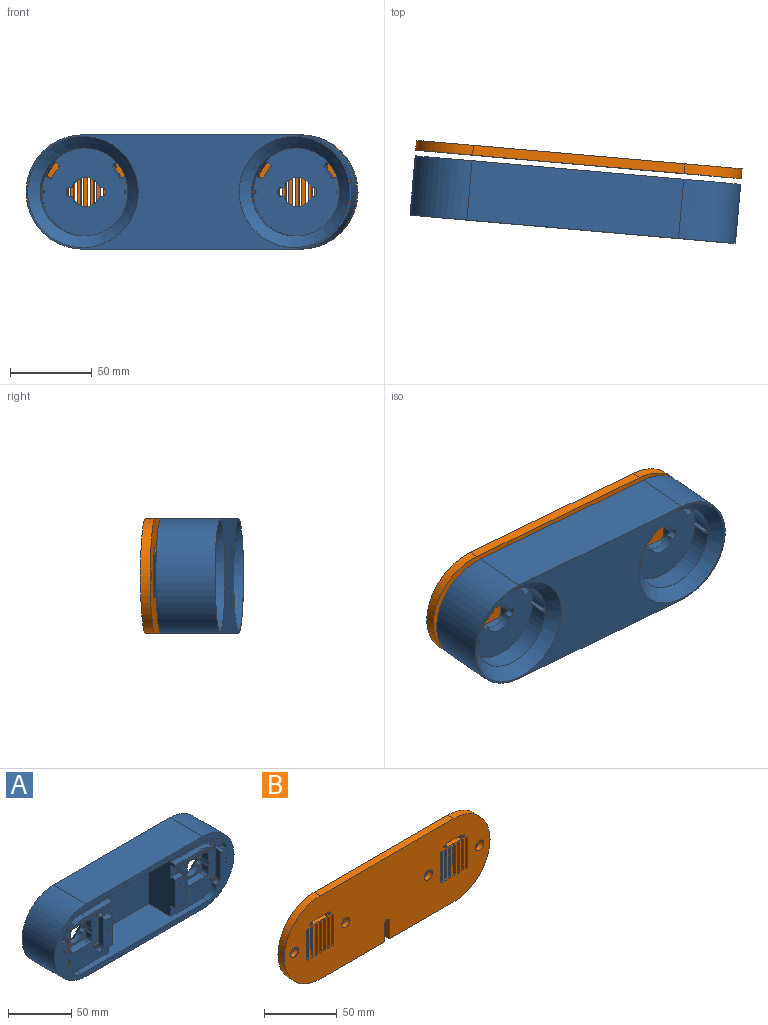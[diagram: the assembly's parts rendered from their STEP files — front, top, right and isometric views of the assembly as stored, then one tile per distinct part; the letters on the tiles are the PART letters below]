
ASSEMBLY  parts=2 mates=1
PART A: 163 faces, bbox 200x36.4x70 mm
  f0: plane 12.01x2.86mm, normal (0.7,0,-0.71), area 45.9mm2, adj f10,f16,f24,f27,f94,f131,f132,f159
  f1: plane 12.01x2.86mm, normal (-0.7,0,-0.71), area 45.9mm2, adj f11,f17,f24,f27,f93,f133,f134,f154
  f2: plane 12.01x2.86mm, normal (0.7,0,-0.71), area 45.9mm2, adj f13,f18,f21,f26,f108,f119,f120,f150
  f3: plane 12.01x2.86mm, normal (-0.7,0,-0.71), area 45.9mm2, adj f15,f19,f21,f26,f105,f123,f124,f145
  f4: plane 41.23x3mm, normal (0,-1,0), area 112.8mm2, adj f8,f78,f147,f148
  f5: plane 30.73x14.5mm, normal (0,-1,0), area 285.2mm2, adj f9,f17,f83,f84,f85,f138,f153
  f6: plane 30.73x14.5mm, normal (0,-1,0), area 285.2mm2, adj f8,f18,f79,f80,f81,f140,f151
  f7: plane 200x70mm, normal (0,-1,0), area 2873.6mm2, adj f16,f19,f37,f38,f39,f40,f70,f71
  f8: plane 60x30.4mm, normal (1,0,0), area 1662.8mm2, adj f4,f6,f26,f73,f78,f81,f82,f90
  f9: plane 60x30.4mm, normal (-1,0,0), area 1662.8mm2, adj f5,f27,f28,f73,f82,f83,f86,f90
  f10: cylinder r=26.5mm len=11.9mm, axis (0,1,0), area 131.3mm2, adj f0,f24,f88,f162
  f11: cylinder r=26.5mm len=11.9mm, axis (0,1,0), area 131.3mm2, adj f1,f12,f24,f155
  f12: plane 11.9x3.74mm, normal (0.36,0,0.93), area 47.6mm2, adj f11,f17,f24,f155
  f13: cylinder r=26.5mm len=11.9mm, axis (0,1,0), area 131.3mm2, adj f2,f14,f21,f152
  f14: plane 11.9x3.74mm, normal (-0.36,0,0.93), area 47.6mm2, adj f13,f18,f21,f152
  f15: cylinder r=26.5mm len=11.9mm, axis (0,1,0), area 131.3mm2, adj f3,f21,f89,f149
  f16: cylinder r=22.5mm len=17.4mm, axis (0,1,0), area 128mm2, adj f0,f7,f24,f27,f87,f88,f94,f131
  f17: cylinder r=22.5mm len=17.4mm, axis (0,1,0), area 128mm2, adj f1,f5,f12,f24,f27,f85,f93,f133
  f18: cylinder r=22.5mm len=17.4mm, axis (0,1,0), area 128mm2, adj f2,f6,f14,f21,f26,f79,f108,f119
  f19: cylinder r=22.5mm len=17.4mm, axis (0,1,0), area 128mm2, adj f3,f7,f21,f26,f77,f89,f105,f123
  f20: cylinder r=27mm len=53.98mm, axis (0,1,0), area 999.9mm2, adj f21,f42,f115,f117
  f21: plane 54x54mm, normal (0,1,0), area 1917.8mm2, adj f2,f3,f13,f14,f15,f18,f19,f20
  f22: cylinder r=27mm len=53.98mm, axis (0,1,0), area 999.9mm2, adj f21,f42,f115,f117
  f23: cylinder r=27mm len=53.98mm, axis (0,1,0), area 999.9mm2, adj f24,f43,f111,f113
  f24: plane 54x54mm, normal (0,1,0), area 1917.8mm2, adj f0,f1,f10,f11,f12,f16,f17,f23
  f25: cylinder r=27mm len=53.98mm, axis (0,1,0), area 999.9mm2, adj f24,f43,f111,f113
  f26: plane 49.5x49.5mm, normal (0,-1,0), area 1345mm2, adj f2,f3,f8,f18,f19,f44,f45,f46
  f27: plane 49.5x49.5mm, normal (0,-1,0), area 1345mm2, adj f0,f1,f9,f16,f17,f58,f59,f60
  f28: plane 41.23x3mm, normal (0,-1,0), area 112.8mm2, adj f9,f86,f156,f157
  f29: cylinder r=3mm len=6mm, axis (0,-1,0), area 52.9mm2, adj f24,f30,f32,f57
  f30: cylinder r=9mm len=17.01mm, axis (0,-1,0), area 111.4mm2, adj f24,f29,f31,f57
  f31: cylinder r=3mm len=6mm, axis (0,-1,0), area 52.9mm2, adj f24,f30,f32,f57
  f32: cylinder r=9mm len=17.01mm, axis (0,-1,0), area 111.4mm2, adj f24,f29,f31,f57
  f33: cylinder r=3mm len=6mm, axis (0,-1,0), area 52.9mm2, adj f21,f34,f36,f56
  f34: cylinder r=9mm len=17.01mm, axis (0,-1,0), area 111.4mm2, adj f21,f33,f35,f56
  f35: cylinder r=3mm len=6mm, axis (0,-1,0), area 52.9mm2, adj f21,f34,f36,f56
  f36: cylinder r=9mm len=17.01mm, axis (0,-1,0), area 111.4mm2, adj f21,f33,f35,f56
  f37: cylinder r=35mm len=70mm, axis (0,-1,0), area 4002.4mm2, adj f7,f38,f40,f41
  f38: plane 130x36.4mm, normal (0,0,-1), area 4732mm2, adj f7,f37,f39,f41
  f39: cylinder r=35mm len=70mm, axis (0,-1,0), area 4002.4mm2, adj f7,f38,f40,f41
  f40: plane 130x36.4mm, normal (0,0,1), area 4732mm2, adj f7,f37,f39,f41
  f41: plane 200x70mm, normal (0,1,0), area 5685.1mm2, adj f37,f38,f39,f40,f42,f43
  f42: cone r=27mm half-angle=45deg, axis (0,1,0), area 1897.1mm2, adj f20,f22,f41,f116,f118
  f43: cone r=27mm half-angle=45deg, axis (0,1,0), area 1897.1mm2, adj f23,f25,f41,f112,f114
  f44: cylinder r=2.7mm len=7mm, axis (0,-1,0), area 29.7mm2, adj f26,f45,f55,f56
  f45: plane 7.5x7mm, normal (1,0,0), area 52.5mm2, adj f26,f44,f46,f56
  f46: cylinder r=3.62mm len=7mm, axis (0,-1,0), area 38.6mm2, adj f26,f45,f47,f56
  f47: plane 7x5.5mm, normal (1,0,0), area 38.5mm2, adj f26,f46,f48,f56
  f48: cylinder r=2.7mm len=7mm, axis (0,-1,0), area 29.7mm2, adj f26,f47,f49,f56
  f49: plane 18x7mm, normal (0,0,1), area 126mm2, adj f26,f48,f50,f56
  f50: cylinder r=2.7mm len=7mm, axis (0,-1,0), area 29.7mm2, adj f26,f49,f51,f56
  f51: plane 7x5.5mm, normal (-1,0,0), area 38.5mm2, adj f26,f50,f52,f56
  f52: cylinder r=3.62mm len=7mm, axis (0,-1,0), area 38.6mm2, adj f26,f51,f53,f56
  f53: plane 7.5x7mm, normal (-1,0,0), area 52.5mm2, adj f26,f52,f54,f56
  f54: cylinder r=2.7mm len=7mm, axis (0,-1,0), area 29.7mm2, adj f26,f53,f55,f56
  f55: plane 18x7mm, normal (0,0,-1), area 126mm2, adj f26,f44,f54,f56
  f56: plane 25.4x23.4mm, normal (0,-1,0), area 262.5mm2, adj f33,f34,f35,f36,f44,f45,f46,f47
  f57: plane 25.4x23.4mm, normal (0,-1,0), area 262.5mm2, adj f29,f30,f31,f32,f58,f59,f60,f61
  f58: cylinder r=2.7mm len=7mm, axis (0,-1,0), area 29.7mm2, adj f27,f57,f59,f69
  f59: plane 18x7mm, normal (0,0,1), area 126mm2, adj f27,f57,f58,f60
  f60: cylinder r=2.7mm len=7mm, axis (0,-1,0), area 29.7mm2, adj f27,f57,f59,f61
  f61: plane 7x5.5mm, normal (-1,0,0), area 38.5mm2, adj f27,f57,f60,f62
  f62: cylinder r=3.62mm len=7mm, axis (0,-1,0), area 38.6mm2, adj f27,f57,f61,f63
  f63: plane 7.5x7mm, normal (-1,0,0), area 52.5mm2, adj f27,f57,f62,f64
  f64: cylinder r=2.7mm len=7mm, axis (0,-1,0), area 29.7mm2, adj f27,f57,f63,f65
  f65: plane 18x7mm, normal (0,0,-1), area 126mm2, adj f27,f57,f64,f66
  f66: cylinder r=2.7mm len=7mm, axis (0,-1,0), area 29.7mm2, adj f27,f57,f65,f67
  f67: plane 7.5x7mm, normal (1,0,0), area 52.5mm2, adj f27,f57,f66,f68
  f68: cylinder r=3.62mm len=7mm, axis (0,-1,0), area 38.6mm2, adj f27,f57,f67,f69
  f69: plane 7x5.5mm, normal (1,0,0), area 38.5mm2, adj f27,f57,f58,f68
  f70: cylinder r=4mm len=5.4mm, axis (0,1,0), area 33.9mm2, adj f7,f27,f71,f87
  f71: plane 5.4x0.5mm, normal (-1,0,0), area 2.7mm2, adj f7,f27,f70,f72
  f72: cylinder r=10mm len=10mm, axis (0,1,0), area 84.8mm2, adj f7,f27,f71,f73
  f73: plane 141x30.4mm, normal (0,0,1), area 2511.4mm2, adj f7,f8,f9,f26,f27,f72,f74,f90
  f74: cylinder r=10mm len=10mm, axis (0,1,0), area 84.8mm2, adj f7,f26,f73,f75
  f75: plane 5.4x0.5mm, normal (1,0,0), area 2.7mm2, adj f7,f26,f74,f76
  f76: cylinder r=4mm len=5.4mm, axis (0,1,0), area 33.9mm2, adj f7,f26,f75,f77
  f77: plane 26.73x5.4mm, normal (1,0,0), area 144.3mm2, adj f7,f19,f26,f76
  f78: plane 41.23x5.5mm, normal (0,0,-1), area 224.1mm2, adj f4,f8,f26,f147,f150,f152
  f79: plane 26.73x5.4mm, normal (-1,0,0), area 144.3mm2, adj f6,f18,f26,f80
  f80: cylinder r=4mm len=5.4mm, axis (0,1,0), area 33.9mm2, adj f6,f26,f79,f81
  f81: plane 14.5x5.4mm, normal (0,0,-1), area 78.3mm2, adj f6,f8,f26,f80
  f82: plane 130x30.4mm, normal (0,0,-1), area 2458mm2, adj f7,f8,f9,f90,f143,f149,f161,f162
  f83: plane 14.5x5.4mm, normal (0,0,-1), area 78.3mm2, adj f5,f9,f27,f84
  f84: cylinder r=4mm len=5.4mm, axis (0,1,0), area 33.9mm2, adj f5,f27,f83,f85
  f85: plane 26.73x5.4mm, normal (1,0,0), area 144.3mm2, adj f5,f17,f27,f84
  f86: plane 41.23x5.5mm, normal (0,0,-1), area 224.1mm2, adj f9,f27,f28,f154,f155,f157
  f87: plane 26.73x5.4mm, normal (-1,0,0), area 144.3mm2, adj f7,f16,f27,f70
  f88: plane 17.4x3.74mm, normal (-0.36,0,0.93), area 69.6mm2, adj f7,f10,f16,f24,f160
  f89: plane 17.4x3.74mm, normal (0.36,0,0.93), area 69.6mm2, adj f7,f15,f19,f21,f144
  f90: plane 70x60mm, normal (0,-1,0), area 4200mm2, adj f8,f9,f73,f82
  f91: cylinder r=2mm len=4mm, axis (0,1,0), area 25.1mm2, adj f27,f92,f93
  f92: plane 4x4mm, normal (0,-1,0), area 9.9mm2, adj f91,f134
  f93: plane 2.33x1.26mm, normal (0,1,0), area 1.7mm2, adj f1,f17,f91,f134
  f94: plane 2.33x1.26mm, normal (0,1,0), area 1.7mm2, adj f0,f16,f95,f132
  f95: cylinder r=2mm len=4mm, axis (0,1,0), area 25.1mm2, adj f27,f94,f96
  f96: plane 4x4mm, normal (0,-1,0), area 9.9mm2, adj f95,f132
  f97: cylinder r=2mm len=4mm, axis (0,1,0), area 25.1mm2, adj f27,f98
  f98: plane 4x4mm, normal (0,-1,0), area 9.9mm2, adj f97,f130
  f99: cylinder r=2mm len=4mm, axis (0,1,0), area 25.1mm2, adj f27,f100
  f100: plane 4x4mm, normal (0,-1,0), area 9.9mm2, adj f99,f128
  f101: cylinder r=2mm len=4mm, axis (0,1,0), area 25.1mm2, adj f26,f102
  f102: plane 4x4mm, normal (0,-1,0), area 9.9mm2, adj f101,f126
  f103: cylinder r=2mm len=4mm, axis (0,1,0), area 25.1mm2, adj f26,f104,f105
  f104: plane 4x4mm, normal (0,-1,0), area 9.9mm2, adj f103,f124
  f105: plane 2.33x1.26mm, normal (0,1,0), area 1.7mm2, adj f3,f19,f103,f124
  f106: cylinder r=2mm len=4mm, axis (0,1,0), area 25.1mm2, adj f26,f107
  f107: plane 4x4mm, normal (0,-1,0), area 9.9mm2, adj f106,f122
  f108: plane 2.33x1.26mm, normal (0,1,0), area 1.7mm2, adj f2,f18,f109,f120
  f109: cylinder r=2mm len=4mm, axis (0,1,0), area 25.1mm2, adj f26,f108,f110
  f110: plane 4x4mm, normal (0,-1,0), area 9.9mm2, adj f109,f120
  f111: extruded ~12x1.99mm, area 57.1mm2, adj f23,f24,f25,f112
  f112: plane 2x1.5mm, normal (0,1,0), area 2.6mm2, adj f43,f111
  f113: extruded ~12x1.99mm, area 57.1mm2, adj f23,f24,f25,f114
  f114: plane 2x1.5mm, normal (0,1,0), area 2.6mm2, adj f43,f113
  f115: extruded ~12x1.99mm, area 57.1mm2, adj f20,f21,f22,f116
  f116: plane 2x1.5mm, normal (0,1,0), area 2.6mm2, adj f42,f115
  f117: extruded ~12x1.99mm, area 57.1mm2, adj f20,f21,f22,f118
  f118: plane 2x1.5mm, normal (0,1,0), area 2.6mm2, adj f42,f117
  f119: cone r=0mm half-angle=59deg, axis (0,-1,0), area 3mm2, adj f2,f18,f120
  f120: cylinder r=0.93mm len=8mm, axis (0,-1,0), area 42.2mm2, adj f2,f18,f108,f110,f119
  f121: cone r=0mm half-angle=59deg, axis (0,-1,0), area 3.1mm2, adj f122
  f122: cylinder r=0.93mm len=8mm, axis (0,-1,0), area 46.5mm2, adj f107,f121
  f123: cone r=0mm half-angle=59deg, axis (0,-1,0), area 3mm2, adj f3,f19,f124
  f124: cylinder r=0.93mm len=8mm, axis (0,-1,0), area 42.2mm2, adj f3,f19,f104,f105,f123
  f125: cone r=0mm half-angle=59deg, axis (0,-1,0), area 3.1mm2, adj f126
  f126: cylinder r=0.93mm len=8mm, axis (0,-1,0), area 46.5mm2, adj f102,f125
  f127: cone r=0mm half-angle=59deg, axis (0,-1,0), area 3.1mm2, adj f128
  f128: cylinder r=0.93mm len=8mm, axis (0,-1,0), area 46.5mm2, adj f100,f127
  f129: cone r=0mm half-angle=59deg, axis (0,-1,0), area 3.1mm2, adj f130
  f130: cylinder r=0.93mm len=8mm, axis (0,-1,0), area 46.5mm2, adj f98,f129
  f131: cone r=0mm half-angle=59deg, axis (0,-1,0), area 3mm2, adj f0,f16,f132
  f132: cylinder r=0.93mm len=8mm, axis (0,-1,0), area 42.2mm2, adj f0,f16,f94,f96,f131
  f133: cone r=0mm half-angle=59deg, axis (0,-1,0), area 3mm2, adj f1,f17,f134
  f134: cylinder r=0.93mm len=8mm, axis (0,-1,0), area 42.2mm2, adj f1,f17,f92,f93,f133
  f135: cone r=0mm half-angle=59deg, axis (0,-1,0), area 11.2mm2, adj f136
  f136: cylinder r=1.75mm len=8.1mm, axis (0,-1,0), area 89.1mm2, adj f7,f135
  f137: cone r=0mm half-angle=59deg, axis (0,-1,0), area 11.2mm2, adj f138
  f138: cylinder r=1.75mm len=8.1mm, axis (0,-1,0), area 89.1mm2, adj f5,f137
  f139: cone r=0mm half-angle=59deg, axis (0,-1,0), area 11.2mm2, adj f140
  f140: cylinder r=1.75mm len=8.1mm, axis (0,-1,0), area 89.1mm2, adj f6,f139
  f141: cone r=0mm half-angle=59deg, axis (0,-1,0), area 11.2mm2, adj f142
  f142: cylinder r=1.75mm len=8.1mm, axis (0,-1,0), area 89.1mm2, adj f7,f141
  f143: cylinder r=30mm len=26.51mm, axis (0,-1,0), area 178.8mm2, adj f7,f82,f144,f149
  f144: cylinder r=3.3mm len=5.5mm, axis (0,-1,0), area 30.7mm2, adj f7,f89,f143,f149
  f145: cylinder r=4mm len=2.93mm, axis (0,-1,0), area 0.3mm2, adj f3,f26,f146,f149
  f146: plane 4.28x0.1mm, normal (0,0,1), area 0.4mm2, adj f26,f145,f147,f149
  f147: cylinder r=22.5mm len=11.23mm, axis (0,-1,0), area 64.6mm2, adj f4,f78,f146,f148,f149
  f148: plane 30x5.5mm, normal (0,0,1), area 165mm2, adj f4,f8,f147,f149
  f149: plane 56.89x20.58mm, normal (0,-1,0), area 406.2mm2, adj f3,f8,f15,f82,f143,f144,f145,f146
  f150: cylinder r=4mm len=2.93mm, axis (0,-1,0), area 0.3mm2, adj f2,f26,f78,f152
  f151: plane 8.97x5.5mm, normal (0,0,1), area 49.3mm2, adj f6,f8,f18,f152
  f152: plane 14.5x11.5mm, normal (0,-1,0), area 92.7mm2, adj f2,f8,f13,f14,f78,f150,f151
  f153: plane 8.97x5.5mm, normal (0,0,1), area 49.3mm2, adj f5,f9,f17,f155
  f154: cylinder r=4mm len=2.93mm, axis (0,-1,0), area 0.3mm2, adj f1,f27,f86,f155
  f155: plane 14.5x11.5mm, normal (0,-1,0), area 92.7mm2, adj f1,f9,f11,f12,f86,f153,f154
  f156: plane 30x5.5mm, normal (0,0,1), area 165mm2, adj f9,f28,f157,f162
  f157: cylinder r=22.5mm len=11.23mm, axis (0,-1,0), area 64.6mm2, adj f28,f86,f156,f158,f162
  f158: plane 4.28x0.1mm, normal (0,0,1), area 0.4mm2, adj f27,f157,f159,f162
  f159: cylinder r=4mm len=2.93mm, axis (0,-1,0), area 0.3mm2, adj f0,f27,f158,f162
  f160: cylinder r=3.3mm len=5.5mm, axis (0,-1,0), area 30.7mm2, adj f7,f88,f161,f162
  f161: cylinder r=30mm len=26.51mm, axis (0,-1,0), area 178.8mm2, adj f7,f82,f160,f162
  f162: plane 56.89x20.58mm, normal (0,-1,0), area 406.2mm2, adj f0,f9,f10,f82,f156,f157,f158,f159
PART B: 94 faces, bbox 200x6x70 mm
  f0: plane 62.5x6mm, normal (0,0,-1), area 375mm2, adj f1,f2,f6,f29
  f1: plane 200x70mm, normal (0,-1,0), area 11843.4mm2, adj f0,f3,f4,f5,f6,f7,f8,f9
  f2: plane 200x70mm, normal (0,1,0), area 11991.6mm2, adj f0,f3,f4,f5,f6,f7,f8,f9
  f3: plane 130x6mm, normal (0,0,1), area 780mm2, adj f1,f2,f4,f6
  f4: cylinder r=35mm len=70mm, axis (0,1,0), area 659.7mm2, adj f1,f2,f3,f5
  f5: plane 62.5x6mm, normal (0,0,-1), area 375mm2, adj f1,f2,f4,f27
  f6: cylinder r=35mm len=70mm, axis (0,1,0), area 659.7mm2, adj f0,f1,f2,f3
  f7: cylinder r=1mm len=6mm, axis (0,1,0), area 18.8mm2, adj f1,f2,f8,f10
  f8: plane 24x6mm, normal (-1,0,0), area 144mm2, adj f1,f2,f7,f9
  f9: cylinder r=1mm len=6mm, axis (0,1,0), area 18.8mm2, adj f1,f2,f8,f10
  f10: plane 24x6mm, normal (1,0,0), area 144mm2, adj f1,f2,f7,f9
  f11: plane 24x6mm, normal (-1,0,0), area 144mm2, adj f1,f2,f12,f13
  f12: cylinder r=1mm len=6mm, axis (0,1,0), area 18.8mm2, adj f1,f2,f11,f14
  f13: cylinder r=1mm len=6mm, axis (0,1,0), area 18.8mm2, adj f1,f2,f11,f14
  f14: plane 24x6mm, normal (1,0,0), area 144mm2, adj f1,f2,f12,f13
  f15: plane 6x3.3mm, normal (-1,0,0), area 19.8mm2, adj f1,f2,f16,f17
  f16: plane 14x6mm, normal (0,0,1), area 84mm2, adj f1,f2,f15,f18
  f17: plane 14x6mm, normal (0,0,-1), area 84mm2, adj f1,f2,f15,f18
  f18: plane 6x3.3mm, normal (1,0,0), area 19.8mm2, adj f1,f2,f16,f17
  f19: cylinder r=1mm len=6mm, axis (0,1,0), area 18.8mm2, adj f1,f2,f20,f22
  f20: plane 24x6mm, normal (-1,0,0), area 144mm2, adj f1,f2,f19,f21
  f21: cylinder r=1mm len=6mm, axis (0,1,0), area 18.8mm2, adj f1,f2,f20,f22
  f22: plane 24x6mm, normal (1,0,0), area 144mm2, adj f1,f2,f19,f21
  f23: cylinder r=1mm len=6mm, axis (0,1,0), area 18.8mm2, adj f1,f2,f24,f26
  f24: plane 24x6mm, normal (-1,0,0), area 144mm2, adj f1,f2,f23,f25
  f25: cylinder r=1mm len=6mm, axis (0,1,0), area 18.8mm2, adj f1,f2,f24,f26
  f26: plane 24x6mm, normal (1,0,0), area 144mm2, adj f1,f2,f23,f25
  f27: plane 15x6mm, normal (1,0,0), area 90mm2, adj f1,f2,f5,f28
  f28: cylinder r=2.5mm len=6mm, axis (0,1,0), area 47.1mm2, adj f1,f2,f27,f29
  f29: plane 15x6mm, normal (-1,0,0), area 90mm2, adj f0,f1,f2,f28
  f30: plane 24x6mm, normal (-1,0,0), area 144mm2, adj f1,f2,f31,f32
  f31: cylinder r=1mm len=6mm, axis (0,1,0), area 18.8mm2, adj f1,f2,f30,f33
  f32: cylinder r=1mm len=6mm, axis (0,1,0), area 18.8mm2, adj f1,f2,f30,f33
  f33: plane 24x6mm, normal (1,0,0), area 144mm2, adj f1,f2,f31,f32
  f34: plane 24x6mm, normal (1,0,0), area 144mm2, adj f1,f2,f35,f37
  f35: cylinder r=1mm len=6mm, axis (0,1,0), area 18.8mm2, adj f1,f2,f34,f36
  f36: plane 24x6mm, normal (-1,0,0), area 144mm2, adj f1,f2,f35,f37
  f37: cylinder r=1mm len=6mm, axis (0,1,0), area 18.8mm2, adj f1,f2,f34,f36
  f38: plane 24x6mm, normal (-1,0,0), area 144mm2, adj f1,f2,f39,f40
  f39: cylinder r=1mm len=6mm, axis (0,1,0), area 18.8mm2, adj f1,f2,f38,f41
  f40: cylinder r=1mm len=6mm, axis (0,1,0), area 18.8mm2, adj f1,f2,f38,f41
  f41: plane 24x6mm, normal (1,0,0), area 144mm2, adj f1,f2,f39,f40
  f42: cylinder r=1mm len=6mm, axis (0,1,0), area 18.8mm2, adj f1,f2,f43,f44
  f43: plane 24x6mm, normal (1,0,0), area 144mm2, adj f1,f2,f42,f45
  f44: plane 24x6mm, normal (-1,0,0), area 144mm2, adj f1,f2,f42,f45
  f45: cylinder r=1mm len=6mm, axis (0,1,0), area 18.8mm2, adj f1,f2,f43,f44
  f46: cylinder r=1mm len=6mm, axis (0,1,0), area 18.8mm2, adj f1,f2,f47,f49
  f47: plane 24x6mm, normal (-1,0,0), area 144mm2, adj f1,f2,f46,f48
  f48: cylinder r=1mm len=6mm, axis (0,1,0), area 18.8mm2, adj f1,f2,f47,f49
  f49: plane 24x6mm, normal (1,0,0), area 144mm2, adj f1,f2,f46,f48
  f50: plane 24x6mm, normal (-1,0,0), area 144mm2, adj f1,f2,f51,f52
  f51: cylinder r=1mm len=6mm, axis (0,1,0), area 18.8mm2, adj f1,f2,f50,f53
  f52: cylinder r=1mm len=6mm, axis (0,1,0), area 18.8mm2, adj f1,f2,f50,f53
  f53: plane 24x6mm, normal (1,0,0), area 144mm2, adj f1,f2,f51,f52
  f54: plane 24x6mm, normal (-1,0,0), area 144mm2, adj f1,f2,f55,f56
  f55: cylinder r=1mm len=6mm, axis (0,1,0), area 18.8mm2, adj f1,f2,f54,f57
  f56: cylinder r=1mm len=6mm, axis (0,1,0), area 18.8mm2, adj f1,f2,f54,f57
  f57: plane 24x6mm, normal (1,0,0), area 144mm2, adj f1,f2,f55,f56
  f58: plane 24x6mm, normal (-1,0,0), area 144mm2, adj f1,f2,f59,f60
  f59: cylinder r=1mm len=6mm, axis (0,1,0), area 18.8mm2, adj f1,f2,f58,f61
  f60: cylinder r=1mm len=6mm, axis (0,1,0), area 18.8mm2, adj f1,f2,f58,f61
  f61: plane 24x6mm, normal (1,0,0), area 144mm2, adj f1,f2,f59,f60
  f62: cylinder r=1mm len=6mm, axis (0,1,0), area 18.8mm2, adj f1,f2,f63,f65
  f63: plane 24x6mm, normal (-1,0,0), area 144mm2, adj f1,f2,f62,f64
  f64: cylinder r=1mm len=6mm, axis (0,1,0), area 18.8mm2, adj f1,f2,f63,f65
  f65: plane 24x6mm, normal (1,0,0), area 144mm2, adj f1,f2,f62,f64
  f66: plane 24x6mm, normal (-1,0,0), area 144mm2, adj f1,f2,f67,f68
  f67: cylinder r=1mm len=6mm, axis (0,1,0), area 18.8mm2, adj f1,f2,f66,f69
  f68: cylinder r=1mm len=6mm, axis (0,1,0), area 18.8mm2, adj f1,f2,f66,f69
  f69: plane 24x6mm, normal (1,0,0), area 144mm2, adj f1,f2,f67,f68
  f70: plane 6x3.3mm, normal (-1,0,0), area 19.8mm2, adj f1,f2,f71,f72
  f71: plane 14x6mm, normal (0,0,1), area 84mm2, adj f1,f2,f70,f73
  f72: plane 14x6mm, normal (0,0,-1), area 84mm2, adj f1,f2,f70,f73
  f73: plane 6x3.3mm, normal (1,0,0), area 19.8mm2, adj f1,f2,f71,f72
  f74: cylinder r=4mm len=8mm, axis (0,-1,0), area 100.5mm2, adj f1,f75
  f75: plane 8x8mm, normal (0,-1,0), area 34.4mm2, adj f74,f85
  f76: cylinder r=4mm len=8mm, axis (0,-1,0), area 100.5mm2, adj f1,f77
  f77: plane 8x8mm, normal (0,-1,0), area 34.4mm2, adj f76,f84
  f78: cylinder r=4mm len=8mm, axis (0,-1,0), area 100.5mm2, adj f1,f79
  f79: plane 8x8mm, normal (0,-1,0), area 34.4mm2, adj f78,f83
  f80: cylinder r=4mm len=8mm, axis (0,-1,0), area 100.5mm2, adj f1,f81
  f81: plane 8x8mm, normal (0,-1,0), area 34.4mm2, adj f80,f82
  f82: cylinder r=2.25mm len=4.5mm, axis (0,1,0), area 28.3mm2, adj f2,f81
  f83: cylinder r=2.25mm len=4.5mm, axis (0,1,0), area 28.3mm2, adj f2,f79
  f84: cylinder r=2.25mm len=4.5mm, axis (0,1,0), area 28.3mm2, adj f2,f77
  f85: cylinder r=2.25mm len=4.5mm, axis (0,1,0), area 28.3mm2, adj f2,f75
  f86: cone r=0mm half-angle=59deg, axis (0,-1,0), area 3.1mm2, adj f87
  f87: cylinder r=0.93mm len=4mm, axis (0,-1,0), area 23.2mm2, adj f1,f86
  f88: cone r=0mm half-angle=59deg, axis (0,-1,0), area 3.1mm2, adj f89
  f89: cylinder r=0.93mm len=4mm, axis (0,-1,0), area 23.2mm2, adj f1,f88
  f90: cone r=0mm half-angle=59deg, axis (0,-1,0), area 3.1mm2, adj f91
  f91: cylinder r=0.93mm len=4mm, axis (0,-1,0), area 23.2mm2, adj f1,f90
  f92: cone r=0mm half-angle=59deg, axis (0,-1,0), area 3.1mm2, adj f93
  f93: cylinder r=0.93mm len=4mm, axis (0,-1,0), area 23.2mm2, adj f1,f92
PLACE A rot(axis=(0,0,1),175deg) t=(1.74,-25.08,7.87)mm
PLACE B rot(axis=(0,0,1),175deg) t=(2.04,-21.63,7.87)mm
MATE slider A.f139 <-> B.f83  axis (0.09,1,0) through (42.05,-23.19,7.87)mm
